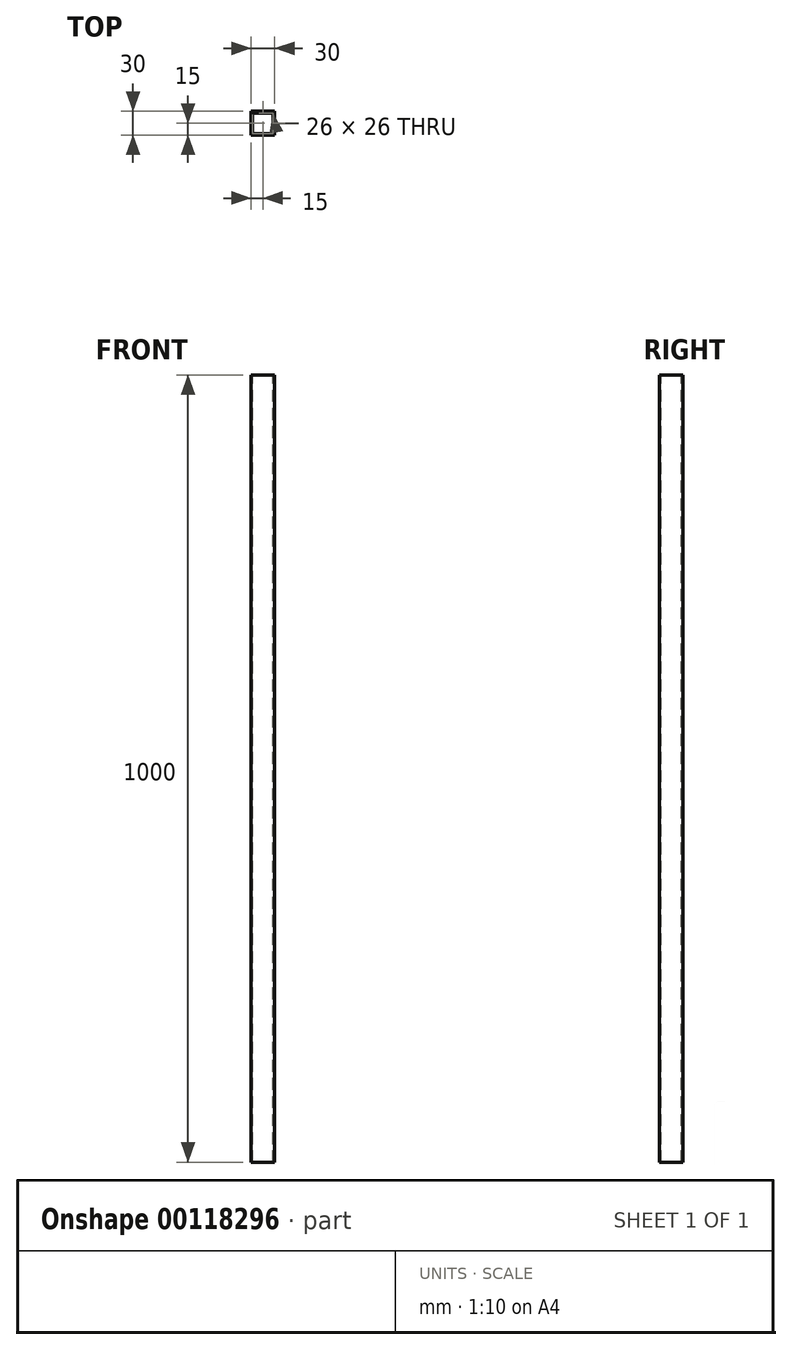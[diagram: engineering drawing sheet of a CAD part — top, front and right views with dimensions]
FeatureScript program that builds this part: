
annotation { "Feature Type Name" : "Feature", "Feature Type Description" : "" }
export const myFeature = defineFeature(function(context is Context, id is Id, definition is map)
    precondition{}
    {
        {
            var Q0;
            Q0=qCreatedBy(makeId("Front.planeOp"),FACE);
            var sketch = newSketch(context, id + "F0", { "sketchPlane" : qUnion([Q0])});
            skLineSegment(sketch, "E0.bottom", {"start": v(15, 500) * mm, "end": v(-15, 500) * mm});
            skLineSegment(sketch, "E0.top", {"start": v(15, -500) * mm, "end": v(-15, -500) * mm});
            skLineSegment(sketch, "E0.left", {"start": v(15, 500) * mm, "end": v(15, -500) * mm});
            skLineSegment(sketch, "E0.right", {"start": v(-15, 500) * mm, "end": v(-15, -500) * mm});
            skPoint(sketch, "E0.middle", {"position": v(0, 0) * mm});
            skSolve(sketch);
        }
        {
            var Q0;
            Q0=makeQuery(id+"F0.imprint","IMPRINT",FACE,{"disambiguationData":[TD([[makeQuery(id+"F0.imprint","IMPRINT",EDGE,{"derivedFrom":sQuery(id+"F0.wireOp",EDGE,"E0.bottom")}),1.0]])]});
            extrude(context, id + "F1", {"entities" : qUnion([Q0]), "depth" : 30 * mm});
        }
        {
            var Q0;
            Q0=makeQuery(id+"F1.opExtrude","SWEPT_FACE",FACE,{"disambiguationData":[OSD([sQuery(id+"F0.wireOp",EDGE,"E0.bottom")])]});
            var sketch = newSketch(context, id + "F2", { "sketchPlane" : qUnion([Q0])});
            skLineSegment(sketch, "E1.0", {"start": v(13, -2) * mm, "end": v(-13, -2) * mm});
            skLineSegment(sketch, "E1.1", {"start": v(13, -28) * mm, "end": v(13, -2) * mm});
            skLineSegment(sketch, "E1.2", {"start": v(-13, -28) * mm, "end": v(13, -28) * mm});
            skLineSegment(sketch, "E1.3", {"start": v(-13, -2) * mm, "end": v(-13, -28) * mm});
            skSolve(sketch);
        }
        {
            var Q0;
            Q0=makeQuery(id+"F2.imprint","IMPRINT",FACE,{"disambiguationData":[TD([[makeQuery(id+"F2.imprint","IMPRINT",EDGE,{"derivedFrom":sQuery(id+"F2.wireOp",EDGE,"E1.0")}),1.0]])]});
            extrude(context, id + "F3", {"entities" : qUnion([Q0]), "operationType" : NewBodyOperationType.REMOVE, "oppositeDirection" : true, "depth" : 1200 * mm});
        }
    });
